# Revit family: 0047911 Sylvania Lighting Fixture ST eco Surface Wall Adj Up & Dwn IP54 290lm 830 WH
name_source: partatom
category: Lighting Fixtures
revit_build: Autodesk Revit 2016 (Build: 20150220_1215(x64)
units: mm (PartAtom-declared; Revit-internal decimal feet)

## family parameters
Cut with Voids When Loaded = No
Host = Face
Light Source = Yes
OmniClass Number = 23.80.70.11.17
OmniClass Title = Specialized Lighting by Location or Use
Part Type = Normal
Room Calculation Point = No
Round Connector Dimension = Use Diameter
Shared = No

## types (1)
- 0047911 ST eco Surface Wall Adj Up & Dwn IP54 290lm 830 WH
    Apparent Load = 5 VA
    Assembly Code = D5020200
    Body Material = Aluminum_Sylvania_Velite_White_RAL 9016
    Catalog Number = 0047911 ST eco Surface Wall Adj Up & Dwn IP54 290lm 830 WH
    Color Filter = 16777215
    Default Elevation = 0 mm  [stored 0 ft]
    Description = A range of sleek and stylish Outdoor LED luminaires.Velite is perfect for lighting courtyards, gardens and exterior entrances.Design  meets IK05 requirements.Available in various shapes, sizes and colours of die cast aluminium luminaires.Range includes bollards and various wall mounted direct and direct/indirect luminaires.High efficient thermal design: ta -20 to +45oC.High performance: delivers up to 830 lm (luminaire lumen output), and up to 71lm/W (total system efficiency).Available in warm white (3,000K).Energy class: A++, A+, A.Lifetime: 30,000 hours life at 70% of the original output L70.
    Diffuser Material = Polycarbonate_Sylvania_Velite_Clear
    Dimming Lamp Color Temperature Shift = <None>
    Drive Current = 300mA
    Electrical Protection = CLASS I
    Energy Class = A++ A+ A
    Height = 108 mm  [stored 0.354331 ft]
    IK Rating = IK05
    IP Rating = IP54
    Lamp = LED
    Lamp Comments = Integrated LED
    Length = 108 mm  [stored 0.354331 ft]
    Life = 25 000h
    Manufacturer = Feilo Sylvania
    Model = ST eco Surface Wall Adj Up & Dwn IP54 290lm 830 WH
    Photometric Web File = 0047911 ST eco Surface Wall Adj Up & Dwn IP54 290lm 830 WH.ies
    Product Page URL = http://www.sylvania-lighting.com
    Rotateable Segment Height = 59 mm  [stored 0.19357 ft]
    Rotateable Segment Width = 34 mm  [stored 0.111549 ft]
    Segment Material = Aluminum_Sylvania_Velite_Black
    Ta Rating = -20°C to +45°C
    Tilt Angle = 0.00°
    URL = http://www.sylvania-lighting.com
    Voltage = 240 V
    Voltage Comments = UNV (Universal Voltage; 230-240 Volt)
    Weight = 0.79 kg
    Width = 108 mm  [stored 0.354331 ft]

note: [stored X ft] marks values corroborated as IEEE doubles in the binary element streams (Revit-internal decimal feet)

## geometry (parser evidence)
native form markers: Blend x5, Sweep x7
no freeform markers — native parametric forms only
